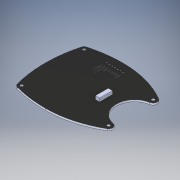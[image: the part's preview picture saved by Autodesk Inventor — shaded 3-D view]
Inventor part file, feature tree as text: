
AUTODESK INVENTOR PART (.ipt)
format: ipt  version: 2018 (Build 220112000, 112)  size: 642,048 bytes
history: native  units: in
note: dims shown in document units (in); Inventor stores cm internally (conversion verified against a paired STEP export)
features: direct_edit x1, emboss x1, sketch x1, imported_body x1, move_body x1
ambient origin geometry x8: Origin, YZ Plane, XZ Plane, XY Plane, X Axis, Y Axis, Z Axis, Center Point
bodies: Solid1 (feature_tree)
feature tree (5):
  direct_edit  "Direct Edit1"
  emboss  "Emboss1"
  sketch  "Sketch1"  dims[d0=0.0in d1=0.0in d2=-0.1875in d3=0.002in d4=0.0in]
  imported_body  "Base1"
  move_body  "Move1"
